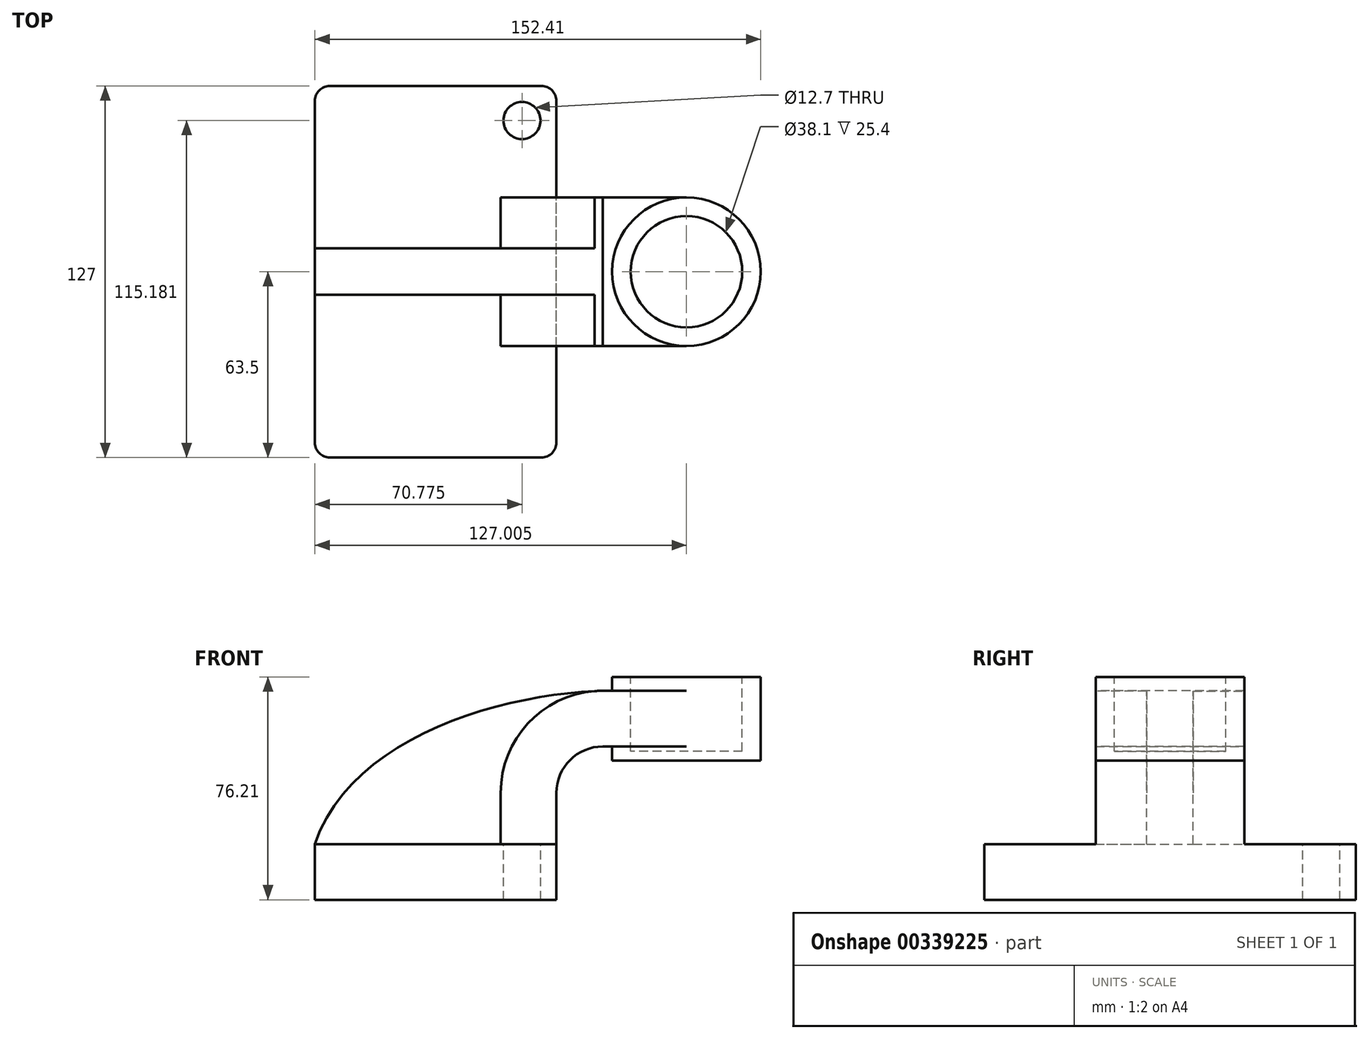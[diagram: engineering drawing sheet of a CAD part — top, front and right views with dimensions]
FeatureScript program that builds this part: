
annotation { "Feature Type Name" : "Feature", "Feature Type Description" : "" }
export const myFeature = defineFeature(function(context is Context, id is Id, definition is map)
    precondition{}
    {
        {
            var Q0;
            Q0=qCreatedBy(makeId("Front.planeOp"),FACE);
            var sketch = newSketch(context, id + "F0", { "sketchPlane" : qUnion([Q0])});
            skLineSegment(sketch, "E0.bottom", {"start": v(41.28, -9.52) * mm, "end": v(-41.28, -9.53) * mm});
            skLineSegment(sketch, "E0.top", {"start": v(41.28, 9.53) * mm, "end": v(-41.28, 9.52) * mm});
            skLineSegment(sketch, "E0.left", {"start": v(41.28, -9.52) * mm, "end": v(41.28, 9.53) * mm});
            skLineSegment(sketch, "E0.right", {"start": v(-41.28, -9.53) * mm, "end": v(-41.28, 9.52) * mm});
            skPoint(sketch, "E0.middle", {"position": v(0, 0) * mm});
            skLineSegment(sketch, "E1.bottom", {"start": v(111.12, 38.1) * mm, "end": v(60.32, 38.1) * mm});
            skLineSegment(sketch, "E1.top", {"start": v(111.13, 66.68) * mm, "end": v(60.33, 66.68) * mm});
            skLineSegment(sketch, "E1.left", {"start": v(111.12, 38.1) * mm, "end": v(111.12, 66.68) * mm});
            skLineSegment(sketch, "E1.right", {"start": v(60.32, 38.1) * mm, "end": v(60.33, 66.68) * mm});
            skPoint(sketch, "E1.middle", {"position": v(85.73, 52.39) * mm});
            skLineSegment(sketch, "E2", {"start": v(41.28, 9.53) * mm, "end": v(41.28, 27) * mm});
            skArc(sketch, "E3", {"start": v(41.28, 27) * mm, "mid": v(45.92, 38.23) * mm, "end": v(57.15, 42.88) * mm});
            skLineSegment(sketch, "E4", {"start": v(57.15, 42.88) * mm, "end": v(85.72, 42.88) * mm});
            skLineSegment(sketch, "E5.0", {"start": v(57.15, 61.93) * mm, "end": v(85.72, 61.93) * mm});
            skArc(sketch, "E5.1", {"start": v(22.23, 27) * mm, "mid": v(32.45, 51.7) * mm, "end": v(57.15, 61.93) * mm});
            skLineSegment(sketch, "E5.2", {"start": v(22.23, 9.53) * mm, "end": v(22.23, 27) * mm});
            skLineSegment(sketch, "E6", {"start": v(85.73, 66.68) * mm, "end": v(85.72, 38.1) * mm});
            skFitSpline(sketch, "E7", {"points": [v(-41.28, 9.52) * mm, v(57.15, 61.93) * mm], "startDerivative": vector(37.78, 111.38) * mm, "endDerivative": vector(102.35, 3.08) * mm});
            skSolve(sketch);
        }
        {
            var Q0;
            Q0=makeQuery(id+"F0.imprint","IMPRINT",FACE,{"disambiguationData":[TD([[makeQuery(id+"F0.imprint","IMPRINT",EDGE,{"derivedFrom":sQuery(id+"F0.wireOp",EDGE,"E0.bottom")}),-1.0]])]});
            extrude(context, id + "F1", {"entities" : qUnion([Q0]), "endBound" : BoundingType.SYMMETRIC, "depth" : 127 * mm});
        }
        {
            var Q0;
            {var subQ1=sQuery(id+"F0.wireOp",EDGE,"E2");Q0=makeQuery(id+"F0.imprint","IMPRINT",FACE,{"disambiguationData":[TD([[makeQuery(id+"F0.imprint","IMPRINT",EDGE,{"derivedFrom":subQ1}),1.0]])]});}
            var Q1;
            {var subQ0=sQuery(id+"F0.wireOp",EDGE,"E4");var subQ1=sQuery(id+"F0.wireOp",EDGE,"E1.right");var subQ2=makeQuery(id+"F0.imprint","INTERSECT",VERTEX,{"derivedFrom":[subQ1,subQ0]});Q1=makeQuery(id+"F0.imprint","IMPRINT",FACE,{"disambiguationData":[TD([[makeQuery(id+"F0.imprint","IMPRINT",EDGE,{"disambiguationData":[TD([[subQ2,-1.0]])],"derivedFrom":subQ1}),-1.0]])]});}
            extrude(context, id + "F2", {"entities" : qUnion([Q0, Q1]), "operationType" : NewBodyOperationType.ADD, "endBound" : BoundingType.SYMMETRIC, "depth" : 50.8 * mm});
        }
        {
            var Q0;
            {var subQ3=sQuery(id+"F0.wireOp",EDGE,"E5.2");Q0=makeQuery(id+"F0.imprint","IMPRINT",FACE,{"disambiguationData":[TD([[makeQuery(id+"F0.imprint","IMPRINT",EDGE,{"derivedFrom":subQ3}),1.0]])]});}
            extrude(context, id + "F3", {"entities" : qUnion([Q0]), "operationType" : NewBodyOperationType.ADD, "endBound" : BoundingType.SYMMETRIC, "depth" : 15.88 * mm});
        }
        {
            var Q0;
            Q0=makeQuery(id+"F1.opExtrude","CAP_EDGE",EDGE,{"disambiguationData":[OSD([sQuery(id+"F0.wireOp",EDGE,"E0.left")])],"isStart":false});
            var Q1;
            Q1=makeQuery(id+"F1.opExtrude","CAP_EDGE",EDGE,{"disambiguationData":[OSD([sQuery(id+"F0.wireOp",EDGE,"E0.right")])],"isStart":false});
            var Q2;
            Q2=makeQuery(id+"F1.opExtrude","CAP_EDGE",EDGE,{"disambiguationData":[OSD([sQuery(id+"F0.wireOp",EDGE,"E0.right")])],"isStart":true});
            var Q3;
            Q3=makeQuery(id+"F1.opExtrude","CAP_EDGE",EDGE,{"disambiguationData":[OSD([sQuery(id+"F0.wireOp",EDGE,"E0.left")])],"isStart":true});
            fillet(context, id + "F4", {"entities" : qUnion([Q0, Q1, Q2, Q3]), "radius" : 5.08 * mm, "tangentPropagation" : true, "allowEdgeOverflow" : false});
        }
        {
            var Q0;
            {var subQ0=sQuery(id+"F0.wireOp",EDGE,"E1.left");Q0=makeQuery(id+"F0.imprint","IMPRINT",FACE,{"disambiguationData":[TD([[makeQuery(id+"F0.imprint","IMPRINT",EDGE,{"derivedFrom":subQ0}),1.0]])]});}
            var Q1;
            Q1=sQuery(id+"F0.wireOp",EDGE,"E6");
            revolve(context, id + "F5", {"operationType" : NewBodyOperationType.ADD, "entities" : qUnion([Q0]), "axis" : qUnion([Q1]), "revolveType" : RevolveType.FULL});
        }
        {
            var Q0;
            {var subQ4=sQuery(id+"F0.wireOp",EDGE,"E0.top");var subQ5=sQuery(id+"F0.wireOp",EDGE,"E0.right");var subQ6=sQuery(id+"F0.wireOp",EDGE,"E0.left");Q0=makeQuery(id+"F3.boolean.opBoolean","SPLIT",FACE,{"disambiguationData":[TD([makeQuery(id+"F1.opExtrude","CAP_FACE",FACE,{"disambiguationData":[OSD([sQuery(id+"F0.wireOp",EDGE,"E0.bottom"),subQ4,subQ6,subQ5])],"isStart":false})])],"derivedFrom":makeQuery(id+"F1.opExtrude","SWEPT_FACE",FACE,{"disambiguationData":[OSD([subQ4])]})});}
            var sketch = newSketch(context, id + "F6", { "sketchPlane" : qUnion([Q0])});
            skCircle(sketch, "E8", {"center": v(29.5, 51.68) * mm, "radius": 6.35 * mm});
            skSolve(sketch);
        }
        {
            var Q0;
            Q0 = qSketchRegion(id + "F6", true);
            extrude(context, id + "F7", {"entities" : qUnion([Q0]), "operationType" : NewBodyOperationType.REMOVE, "endBound" : BoundingType.SYMMETRIC, "oppositeDirection" : true, "depth" : 101.6 * mm});
        }
        {
            var Q0;
            Q0=makeQuery(id+"F5.opRevolve","SWEPT_FACE",FACE,{"disambiguationData":[OSD([sQuery(id+"F0.wireOp",EDGE,"E1.top")])]});
            var sketch = newSketch(context, id + "F8", { "sketchPlane" : qUnion([Q0])});
            skCircle(sketch, "E9", {"center": v(85.72, 0) * mm, "radius": 19.05 * mm});
            skSolve(sketch);
        }
        {
            var Q0;
            Q0=makeQuery(id+"F8.imprint","IMPRINT",FACE,{"disambiguationData":[TD([[makeQuery(id+"F8.imprint","IMPRINT",EDGE,{"derivedFrom":sQuery(id+"F8.wireOp",EDGE,"E9")}),1.0]])]});
            extrude(context, id + "F9", {"entities" : qUnion([Q0]), "operationType" : NewBodyOperationType.REMOVE, "oppositeDirection" : true, "depth" : 25.4 * mm});
        }
    });
